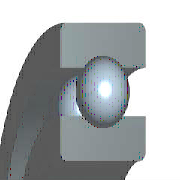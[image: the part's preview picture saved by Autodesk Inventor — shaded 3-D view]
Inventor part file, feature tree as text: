
AUTODESK INVENTOR PART (.ipt)
format: ipt  version: 2023.1 (Build 271208000, 208)  size: 335,360 bytes
history: native  units: mm (DEFAULTED — no unit token found)
features: sketch x5, other x3, plane x2, pattern_circular x1, fillet x1
ambient origin geometry x8: Origin, YZ Plane, XZ Plane, XY Plane, X Axis, Y Axis, Z Axis, Center Point
bodies: Solid1 (feature_tree)
feature tree (12):
  sketch  "Sketch1"  dims[d2=72.0mm]
  other  "WorkPoint1"
  other  "WorkAxis1"
  plane  "WorkPlane3"
  plane  "WorkPlane4"
  sketch  "Sketch4"  dims[d5=12.0mm]
  other  "WorkPoint2"
  pattern_circular  "PolarArray1"  Count=2  [1 undecoded]
  fillet  "Fillet1"  Radius=25.0mm
  sketch  "Sketch2"  dims[d3=47.0mm]
  sketch  "Sketch3"  dims[d4=19.0mm]
  sketch  "Sketch5"  dims[d6=360.0deg d7=0.0mm d8=15.6mm d9=6.6mm d10=360.0deg d11=-12.0mm d12=0.0mm d13=0.0mm d14=15.6001mm d15=6.6001mm d16=360.0deg d17=85.818182mm d19=360.0deg d20=0.6mm d21=16.02mm d22=18.0mm d23=19.98mm d26=0.0mm d27=0.0mm d28=0.0mm d29=0.0mm d30=0.0mm]
note: 1 required parameter value undecoded (feature->parameter linkage not recoverable at this tier; creation-order binding heuristic only, values carry confidence <= 0.55)
